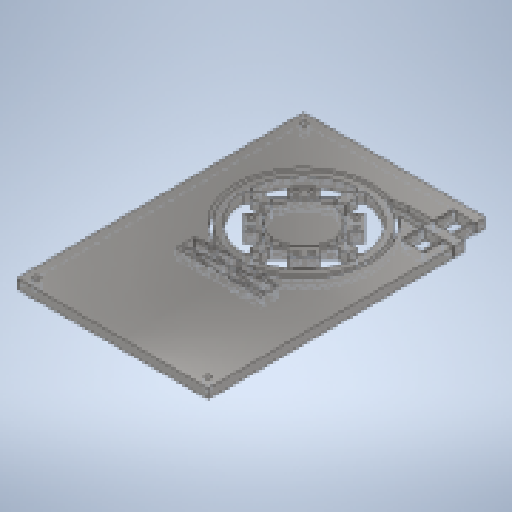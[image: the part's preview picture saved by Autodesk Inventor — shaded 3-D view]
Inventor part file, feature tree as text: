
AUTODESK INVENTOR PART (.ipt)
format: ipt  version: 2023 (Build 270158000, 158)  size: 747,520 bytes
history: native  units: mm
features: extrude x10, sketch x10, other x1
ambient origin geometry x8: Origin, YZ Plane, XZ Plane, XY Plane, X Axis, Y Axis, Z Axis, Center Point
bodies: Solid1 (feature_tree)
feature tree (21):
  other  "<userpath>\OneDrive\ClawdDrive\Objet3D\IminaProbe\Settings.xlsx"
  extrude  "Extrusion1"  Depth=100.0mm
  extrude  "Extrusion6"  TaperAngle=0.0deg  [1 undecoded]
  extrude  "Extrusion7"  Depth=1.0mm
  extrude  "Extrusion10"  Depth=1.0mm
  extrude  "Extrusion11"  Depth=50.0mm
  extrude  "Extrusion12"  Depth=30.0mm
  extrude  "Extrusion13"  Depth=67.082039mm
  extrude  "Extrusion14"  Depth=0.5mm
  extrude  "Extrusion15"  Depth=5.0mm
  extrude  "Extrusion16"  Depth=5.0mm
  sketch  "Sketch1"  dims[d0=150.0mm d1=100.0mm]
  sketch  "Sketch6"  dims[d2=5.0mm d3=0.0mm]
  sketch  "Sketch7"  dims[d14=1.0mm d16=1.0mm]
  sketch  "Sketch9"  dims[d19=1.0mm d23=52.849025mm d24=57.849025mm]
  sketch  "Sketch11"  dims[d25=67.849025mm]
  sketch  "Sketch12"  dims[d31=45.0deg d32=45.0deg d33=45.0deg d34=45.0deg d40=45.0deg d45=45.0deg d46=45.0deg d47=45.0deg d78=50.0mm]
  sketch  "Sketch13"  dims[d79=50.0mm d80=30.0mm]
  sketch  "Sketch14"  dims[d81=60.0mm d82=67.082039mm]
  sketch  "Sketch15"  dims[d83=0.5mm d84=0.5mm]
  sketch  "Sketch16"  dims[d91=72.082039mm d92=5.0mm d93=2.5mm d94=2.5mm d95=45.0deg d96=45.0deg d97=0.5mm d98=0.5mm d99=0.5mm d100=45.0deg d101=45.0deg d102=6.0mm d103=7.0mm d104=3.0mm d105=3.0mm d106=3.0mm d107=3.0mm d108=7.5mm d109=3.0mm d110=6.0mm d111=7.0mm d112=3.0mm d113=3.0mm d114=3.0mm d115=40.0mm d117=360.0deg d119=10.0mm d120=0.0mm d125=45.0deg d128=10.0mm d133=12.0mm d134=12.0mm d135=5.0mm d136=1.0mm d137=1.0mm d138=1.0mm d139=1.0mm d140=0.5mm d141=0.5mm d142=11.0mm d144=11.0mm d145=11.0mm d146=10.0mm d147=11.0mm d154=5.0mm d155=0.0mm d164=5.0mm d167=5.0mm d168=1.0mm d169=0.0mm d170=5.0mm d171=1.0mm d172=2.0mm d179=1.0mm d180=1.0mm d182=1.013794mm d183=20.0mm d185=6.013794mm d186=10.0mm d188=10.0mm d190=1.0mm d191=1.0mm d200=5.0mm d201=0.0mm d202=5.0mm d203=0.0mm d204=1.0mm d205=1.0mm d206=1.0mm d207=1.0mm d208=5.0mm d209=5.0mm d214=3.0mm d220=67.082039mm d221=5.0mm d222=0.0mm d223=5.0mm d224=0.0mm d225=5.0mm d226=0.0mm d227=5.0mm d228=5.0mm d229=5.0mm d230=5.0mm d231=5.0mm d232=5.0mm d233=3.0mm d234=3.0mm d235=3.0mm d236=5.0mm d237=0.0mm d238=2.0mm d239=2.0mm d240=0.7mm d241=4.3mm d243=1.0mm d244=3.0mm d245=3.0mm d246=0.5mm d247=4.3mm d248=4.3mm d249=2.2mm d250=2.2mm d251=40.0mm d253=360.0deg d255=5.0mm d256=0.0mm d257=40.0mm d259=360.0deg d261=5.0mm d262=0.0mm d258=0.872665mm d260=0.872665mm]
note: 1 required parameter value undecoded (feature->parameter linkage not recoverable at this tier; creation-order binding heuristic only, values carry confidence <= 0.55)
